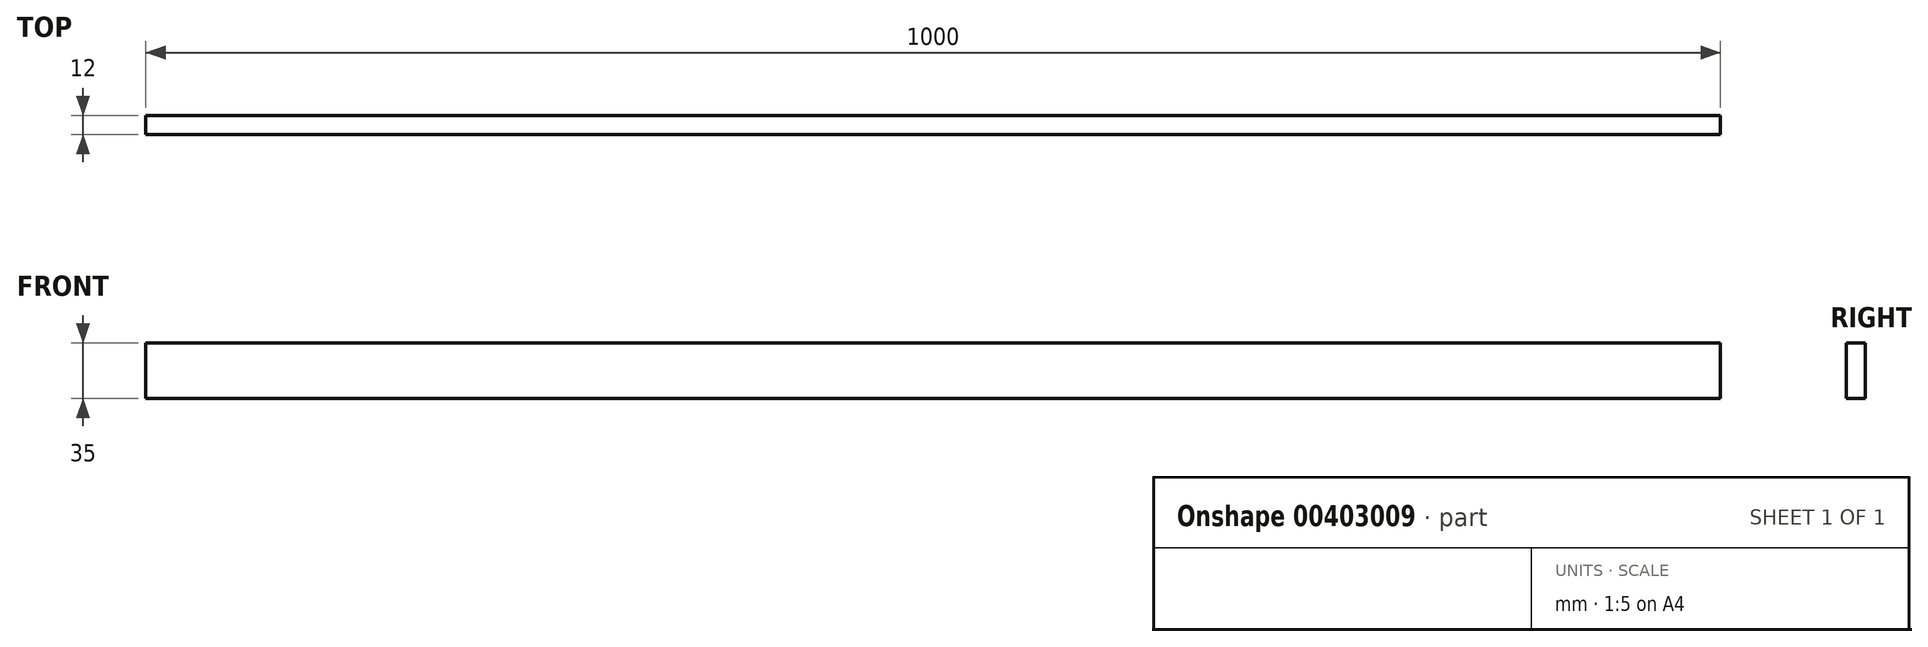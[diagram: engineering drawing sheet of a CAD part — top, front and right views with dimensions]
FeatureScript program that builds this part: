
annotation { "Feature Type Name" : "Feature", "Feature Type Description" : "" }
export const myFeature = defineFeature(function(context is Context, id is Id, definition is map)
    precondition{}
    {
        {
            var Q0;
            Q0=qCreatedBy(makeId("Front.planeOp"),FACE);
            var sketch = newSketch(context, id + "F0", { "sketchPlane" : qUnion([Q0])});
            skLineSegment(sketch, "E0.bottom", {"start": v(0, 0) * mm, "end": v(1000, 0) * mm});
            skLineSegment(sketch, "E0.top", {"start": v(0, 35) * mm, "end": v(1000, 35) * mm});
            skLineSegment(sketch, "E0.left", {"start": v(0, 0) * mm, "end": v(0, 35) * mm});
            skLineSegment(sketch, "E0.right", {"start": v(1000, 0) * mm, "end": v(1000, 35) * mm});
            skSolve(sketch);
        }
        {
            var Q0;
            Q0=makeQuery(id+"F0.imprint","IMPRINT",FACE,{"disambiguationData":[TD([[makeQuery(id+"F0.imprint","IMPRINT",EDGE,{"derivedFrom":sQuery(id+"F0.wireOp",EDGE,"ESCJjQW9-Kipg-MWqb-1C1w-8BTgatxLSc3F.bottom")}),1.0]])]});
            var Q1;
            Q1=makeQuery(id+"F0.imprint","IMPRINT",FACE,{"disambiguationData":[TD([[makeQuery(id+"F0.imprint","IMPRINT",EDGE,{"derivedFrom":sQuery(id+"F0.wireOp",EDGE,"E0.bottom")}),1.0]])]});
            extrude(context, id + "F1", {"entities" : qUnion([Q0, Q1]), "depth" : 12 * mm});
        }
    });
